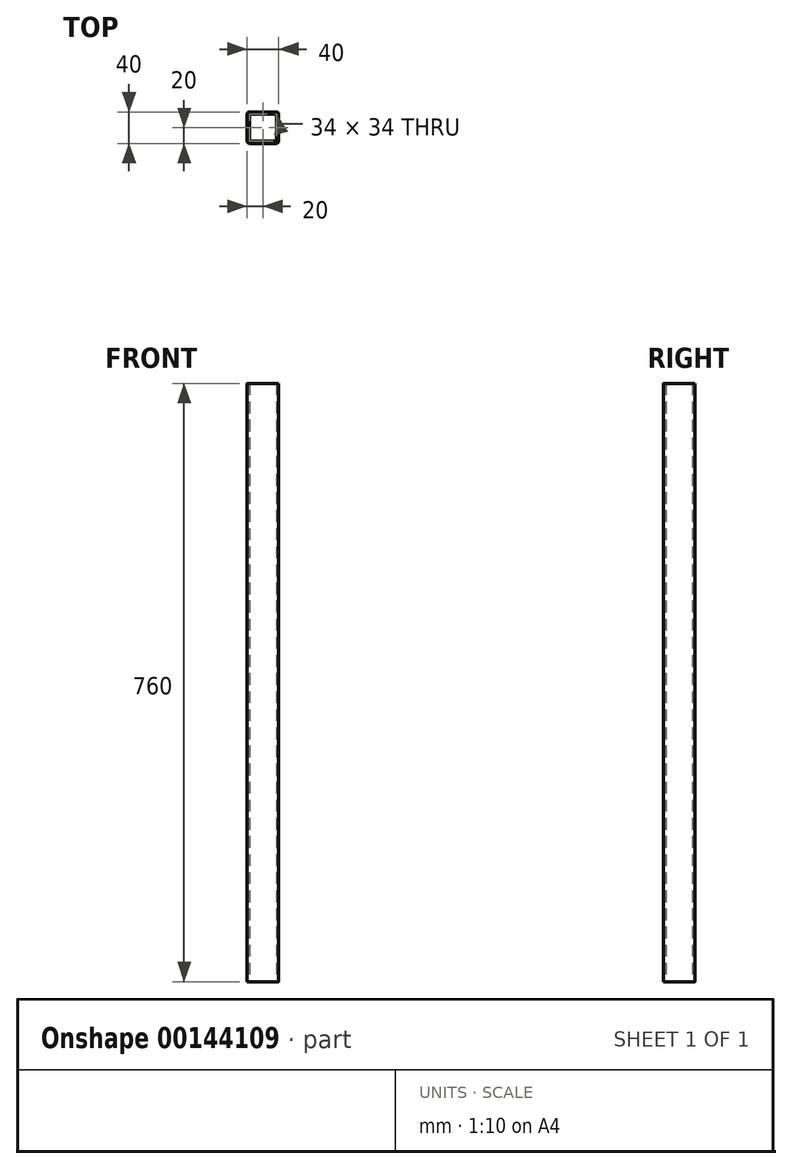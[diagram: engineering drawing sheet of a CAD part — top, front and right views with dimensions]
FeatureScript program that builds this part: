
annotation { "Feature Type Name" : "Feature", "Feature Type Description" : "" }
export const myFeature = defineFeature(function(context is Context, id is Id, definition is map)
    precondition{}
    {
        {
            var Q0;
            Q0=qCreatedBy(makeId("Top.planeOp"),FACE);
            var sketch = newSketch(context, id + "F0", { "sketchPlane" : qUnion([Q0])});
            skLineSegment(sketch, "E0.bottom", {"start": v(17, 20) * mm, "end": v(-17, 20) * mm});
            skLineSegment(sketch, "E0.top", {"start": v(17, -20) * mm, "end": v(-17, -20) * mm});
            skLineSegment(sketch, "E0.left", {"start": v(20, 17) * mm, "end": v(20, -17) * mm});
            skLineSegment(sketch, "E0.right", {"start": v(-20, 17) * mm, "end": v(-20, -17) * mm});
            skPoint(sketch, "E0.middle", {"position": v(0, 0) * mm});
            skPoint(sketch, "E1.visualSharp", {"position": v(-20, 20) * mm});
            skArc(sketch, "E1.filletArc", {"start": v(-17, 20) * mm, "mid": v(-19.12, 19.12) * mm, "end": v(-20, 17) * mm});
            skPoint(sketch, "E2.visualSharp", {"position": v(20, 20) * mm});
            skArc(sketch, "E2.filletArc", {"start": v(20, 17) * mm, "mid": v(19.12, 19.12) * mm, "end": v(17, 20) * mm});
            skPoint(sketch, "E3.visualSharp", {"position": v(20, -20) * mm});
            skArc(sketch, "E3.filletArc", {"start": v(17, -20) * mm, "mid": v(19.12, -19.12) * mm, "end": v(20, -17) * mm});
            skPoint(sketch, "E4.visualSharp", {"position": v(-20, -20) * mm});
            skArc(sketch, "E4.filletArc", {"start": v(-20, -17) * mm, "mid": v(-19.12, -19.12) * mm, "end": v(-17, -20) * mm});
            skLineSegment(sketch, "E5.0", {"start": v(17, 17) * mm, "end": v(-17, 17) * mm});
            skLineSegment(sketch, "E5.1", {"start": v(17, 17) * mm, "end": v(17, -17) * mm});
            skLineSegment(sketch, "E5.2", {"start": v(17, -17) * mm, "end": v(-17, -17) * mm});
            skLineSegment(sketch, "E5.3", {"start": v(-17, 17) * mm, "end": v(-17, -17) * mm});
            skSolve(sketch);
        }
        {
            var Q0;
            Q0=makeQuery(id+"F0.imprint","IMPRINT",FACE,{"disambiguationData":[TD([[makeQuery(id+"F0.imprint","IMPRINT",EDGE,{"derivedFrom":sQuery(id+"F0.wireOp",EDGE,"E0.bottom")}),1.0]])]});
            extrude(context, id + "F1", {"entities" : qUnion([Q0]), "depth" : 760 * mm});
        }
    });
